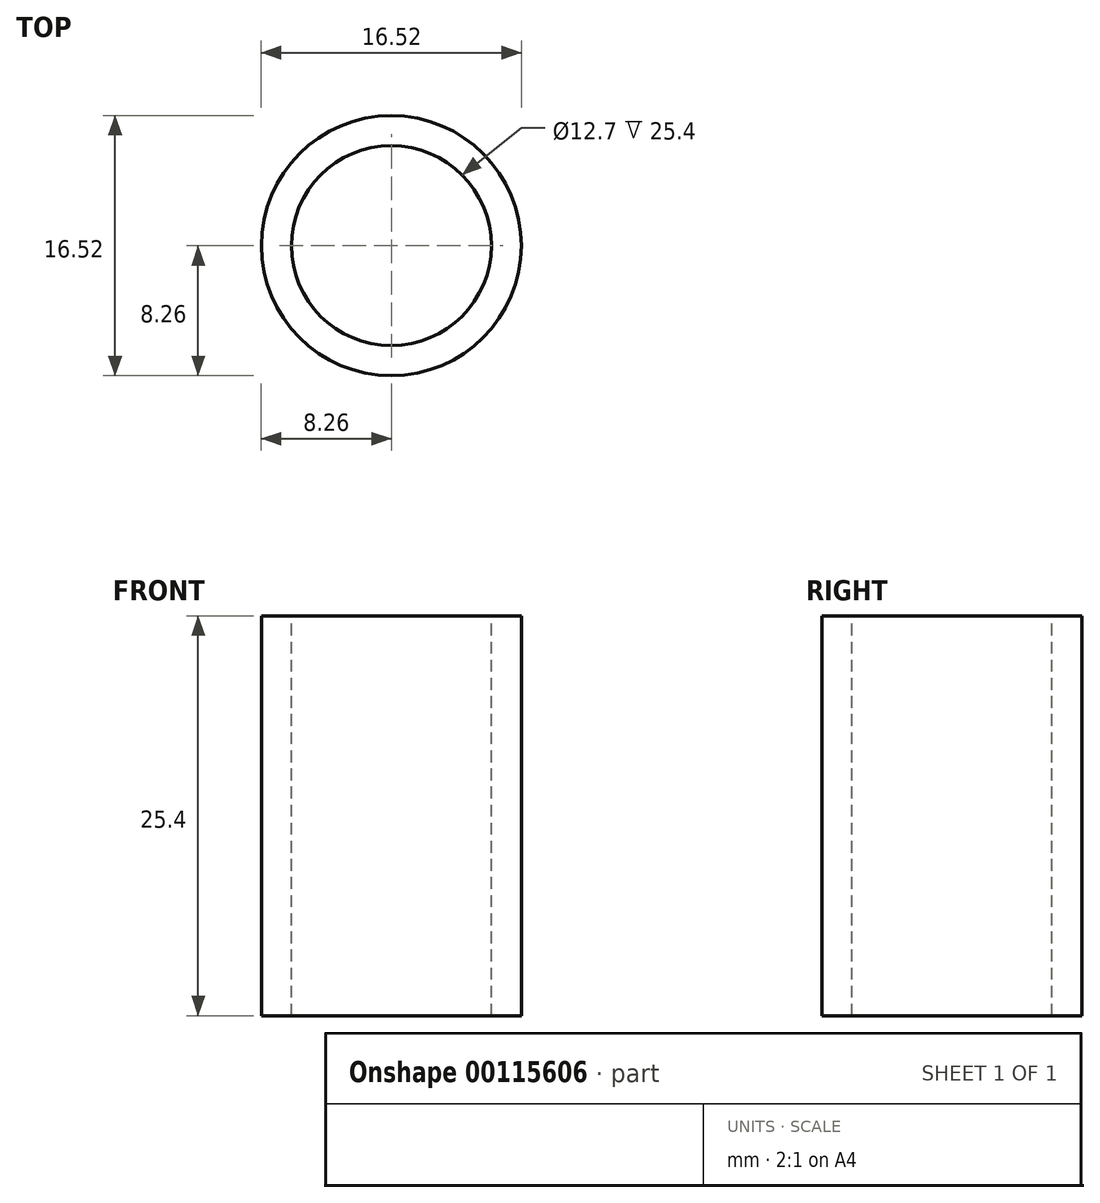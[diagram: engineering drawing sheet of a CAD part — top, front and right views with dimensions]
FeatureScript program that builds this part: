
annotation { "Feature Type Name" : "Feature", "Feature Type Description" : "" }
export const myFeature = defineFeature(function(context is Context, id is Id, definition is map)
    precondition{}
    {
        {
            var Q0;
            Q0=qCreatedBy(makeId("Top.planeOp"),FACE);
            var sketch = newSketch(context, id + "F0", { "sketchPlane" : qUnion([Q0])});
            skCircle(sketch, "E0", {"center": v(0, 0) * mm, "radius": 8.26 * mm});
            skSolve(sketch);
        }
        {
            var Q0;
            Q0=makeQuery(id+"F0.imprint","IMPRINT",FACE,{"disambiguationData":[TD([[makeQuery(id+"F0.imprint","IMPRINT",EDGE,{"derivedFrom":sQuery(id+"F0.wireOp",EDGE,"E0")}),1.0]])]});
            extrude(context, id + "F1", {"entities" : qUnion([Q0]), "depth" : 25.4 * mm});
        }
        {
            var Q0;
            Q0=makeQuery(id+"F1.opExtrude","CAP_FACE",FACE,{"disambiguationData":[OSD([sQuery(id+"F0.wireOp",EDGE,"E0")])],"isStart":false});
            var sketch = newSketch(context, id + "F2", { "sketchPlane" : qUnion([Q0])});
            skPoint(sketch, "E1", {"position": v(0, 0) * mm});
            skSolve(sketch);
        }
        {
            var Q0;
            Q0=sQuery(id+"F2.wireOp",VERTEX,"E1");
            var Q1;
            Q1=makeQuery(id+"F1.opExtrude","SWEPT_BODY",BODY,{"disambiguationData":[OSD([sQuery(id+"F0.wireOp",EDGE,"E0")])]});
            hole(context, id + "F3", {"style" : HoleStyle.SIMPLE, "endStyle" : HoleEndStyle.THROUGH, "holeDiameter" : 12.7 * mm, "locations" : qUnion([Q0]), "scope" : qUnion([Q1]), "isTappedThrough" : true});
        }
    });
